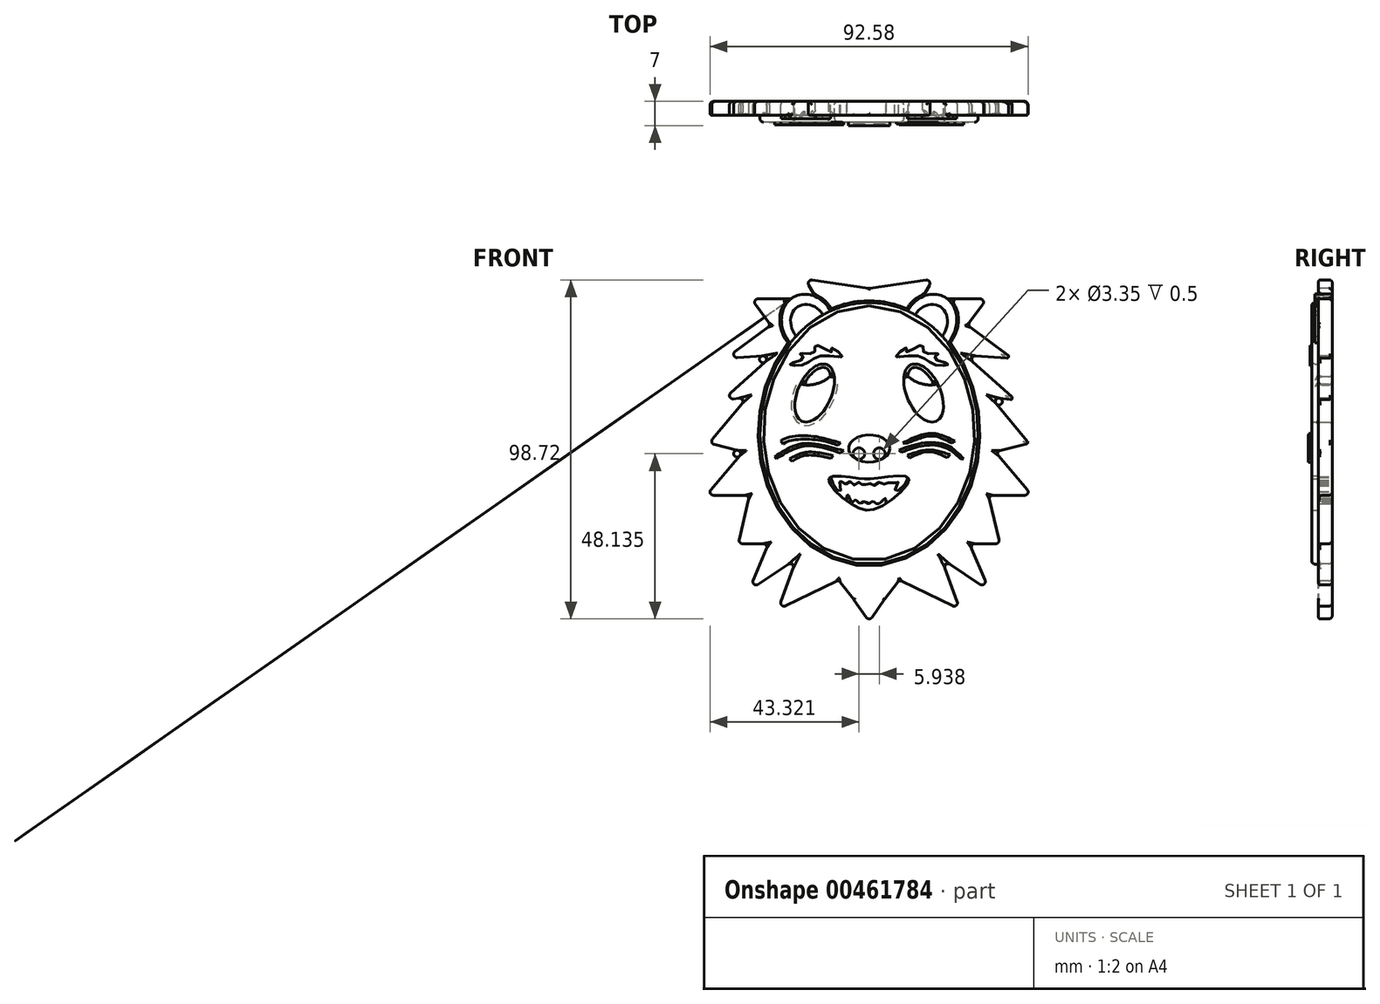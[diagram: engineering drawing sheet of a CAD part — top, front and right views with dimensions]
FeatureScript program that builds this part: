
annotation { "Feature Type Name" : "Feature", "Feature Type Description" : "" }
export const myFeature = defineFeature(function(context is Context, id is Id, definition is map)
    precondition{}
    {
        {
            var Q0;
            Q0=qCreatedBy(makeId("Front.planeOp"),FACE);
            var sketch = newSketch(context, id + "F0", { "sketchPlane" : qUnion([Q0])});
            skEllipse(sketch, "E0", {"center": v(0, 0) * mm, "majorRadius": 38.1 * mm, "minorRadius": 31.75 * mm, "majorAxis": v(0, 1)});
            skSolve(sketch);
        }
        {
            var Q0;
            Q0 = qSketchRegion(id + "F0", true);
            extrude(context, id + "F1", {"entities" : qUnion([Q0]), "depth" : 6 * mm});
        }
        {
            var Q0;
            Q0=makeQuery(id+"F1.opExtrude","CAP_FACE",FACE,{"disambiguationData":[OSD([sQuery(id+"F0.wireOp",EDGE,"E0")])],"isStart":false});
            var sketch = newSketch(context, id + "F2", { "sketchPlane" : qUnion([Q0])});
            skEllipse(sketch, "E1", {"center": v(-15.85, 11.73) * mm, "majorRadius": 9 * mm, "minorRadius": 4.9 * mm, "majorAxis": v(0.4, 0.91)});
            skEllipse(sketch, "E2.MirrorC", {"center": v(15.85, 11.73) * mm, "majorRadius": 9 * mm, "minorRadius": 4.9 * mm, "majorAxis": v(-0.4, 0.91)});
            skSolve(sketch);
        }
        {
            var Q0;
            Q0 = qSketchRegion(id + "F2", true);
            extrude(context, id + "F3", {"entities" : qUnion([Q0]), "operationType" : NewBodyOperationType.REMOVE, "oppositeDirection" : true, "depth" : 6 * mm});
        }
        {
            var Q0;
            Q0=qCreatedBy(makeId("Front.planeOp"),FACE);
            var sketch = newSketch(context, id + "F4", { "sketchPlane" : qUnion([Q0])});
            skEllipse(sketch, "E3", {"center": v(0, -4.43) * mm, "majorRadius": 6 * mm, "minorRadius": 4 * mm, "majorAxis": v(1, 0)});
            skSolve(sketch);
        }
        {
            var Q0;
            Q0 = qSketchRegion(id + "F4", true);
            extrude(context, id + "F5", {"entities" : qUnion([Q0]), "operationType" : NewBodyOperationType.ADD, "depth" : 7 * mm});
        }
        {
            var Q0;
            Q0=qCreatedBy(makeId("Front.planeOp"),FACE);
            var sketch = newSketch(context, id + "F6", { "sketchPlane" : qUnion([Q0])});
            skLineSegment(sketch, "E4", {"start": v(-18.6, 44.96) * mm, "end": v(-15.24, 39.17) * mm});
            skLineSegment(sketch, "E5", {"start": v(-15.24, 39.17) * mm, "end": v(-34.29, 39.17) * mm});
            skLineSegment(sketch, "E6", {"start": v(-34.29, 39.17) * mm, "end": v(-28.63, 31.48) * mm});
            skLineSegment(sketch, "E7", {"start": v(-28.63, 31.48) * mm, "end": v(-41.79, 21.8) * mm});
            skLineSegment(sketch, "E8", {"start": v(-41.79, 21.8) * mm, "end": v(-28.04, 22.78) * mm});
            skLineSegment(sketch, "E9", {"start": v(-28.04, 22.78) * mm, "end": v(-42.7, 9.6) * mm});
            skLineSegment(sketch, "E10", {"start": v(-42.7, 9.6) * mm, "end": v(-35.36, 10.58) * mm});
            skLineSegment(sketch, "E11", {"start": v(-35.36, 10.58) * mm, "end": v(-46.61, -2.9) * mm});
            skLineSegment(sketch, "E12", {"start": v(-46.61, -2.9) * mm, "end": v(-36.6, -5.33) * mm});
            skLineSegment(sketch, "E13", {"start": v(-36.6, -5.33) * mm, "end": v(-47.45, -18.05) * mm});
            skLineSegment(sketch, "E14", {"start": v(-38.1, -32.16) * mm, "end": v(-29.26, -32.16) * mm});
            skLineSegment(sketch, "E15", {"start": v(-29.26, -32.16) * mm, "end": v(-35.05, -45.87) * mm});
            skLineSegment(sketch, "E16", {"start": v(-35.05, -45.87) * mm, "end": v(-21.03, -36.42) * mm});
            skLineSegment(sketch, "E17", {"start": v(-21.03, -36.42) * mm, "end": v(-26.52, -51.36) * mm});
            skLineSegment(sketch, "E18", {"start": v(-26.52, -51.36) * mm, "end": v(-8.87, -42.69) * mm});
            skLineSegment(sketch, "E19", {"start": v(-8.87, -42.69) * mm, "end": v(-4.45, -48.4) * mm});
            skLineSegment(sketch, "E20", {"start": v(-4.45, -48.4) * mm, "end": v(0, -54.8) * mm});
            skLineSegment(sketch, "E21", {"start": v(0, -38.1) * mm, "end": v(-21.95, -23.62) * mm});
            skLineSegment(sketch, "E22", {"start": v(-21.95, -23.62) * mm, "end": v(-29.26, 0) * mm});
            skPoint(sketch, "E22.endSnap0", {"position": v(-31.75, 0) * mm});
            skLineSegment(sketch, "E23", {"start": v(-29.26, 0) * mm, "end": v(-24.03, 24.9) * mm});
            skLineSegment(sketch, "E24", {"start": v(-24.03, 24.9) * mm, "end": v(-8.87, 36.06) * mm});
            skLineSegment(sketch, "E25", {"start": v(-8.87, 36.06) * mm, "end": v(0, 38.1) * mm});
            skLineSegment(sketch, "E26", {"start": v(-47.45, -18.05) * mm, "end": v(-34.77, -18.05) * mm});
            skLineSegment(sketch, "E27", {"start": v(-34.77, -18.05) * mm, "end": v(-38.1, -32.16) * mm});
            skLineSegment(sketch, "E28.MirrorCS", {"start": v(18.6, 44.96) * mm, "end": v(15.24, 39.17) * mm});
            skLineSegment(sketch, "E29.MirrorCS", {"start": v(15.24, 39.17) * mm, "end": v(34.29, 39.17) * mm});
            skLineSegment(sketch, "E30.MirrorCS", {"start": v(34.29, 39.17) * mm, "end": v(28.63, 31.48) * mm});
            skLineSegment(sketch, "E31.MirrorCS", {"start": v(28.63, 31.48) * mm, "end": v(41.79, 21.8) * mm});
            skLineSegment(sketch, "E32.MirrorCS", {"start": v(41.79, 21.8) * mm, "end": v(28.04, 22.78) * mm});
            skLineSegment(sketch, "E33.MirrorCS", {"start": v(28.04, 22.78) * mm, "end": v(42.7, 9.6) * mm});
            skLineSegment(sketch, "E34.MirrorCS", {"start": v(42.7, 9.6) * mm, "end": v(35.36, 10.58) * mm});
            skLineSegment(sketch, "E35.MirrorCS", {"start": v(35.36, 10.58) * mm, "end": v(46.61, -2.9) * mm});
            skLineSegment(sketch, "E36.MirrorCS", {"start": v(36.6, -5.33) * mm, "end": v(47.45, -18.05) * mm});
            skLineSegment(sketch, "E37.MirrorCS", {"start": v(47.45, -18.05) * mm, "end": v(34.77, -18.05) * mm});
            skLineSegment(sketch, "E38.MirrorCS", {"start": v(38.1, -32.16) * mm, "end": v(29.26, -32.16) * mm});
            skLineSegment(sketch, "E39.MirrorCS", {"start": v(29.26, -32.16) * mm, "end": v(35.05, -45.87) * mm});
            skLineSegment(sketch, "E40.MirrorCS", {"start": v(35.05, -45.87) * mm, "end": v(21.03, -36.42) * mm});
            skLineSegment(sketch, "E41.MirrorCS", {"start": v(21.03, -36.42) * mm, "end": v(26.52, -51.36) * mm});
            skLineSegment(sketch, "E42.MirrorCS", {"start": v(26.52, -51.36) * mm, "end": v(8.87, -42.69) * mm});
            skLineSegment(sketch, "E43.MirrorCS", {"start": v(4.45, -48.4) * mm, "end": v(0, -54.8) * mm});
            skLineSegment(sketch, "E44.MirrorCS", {"start": v(8.87, -42.69) * mm, "end": v(4.45, -48.4) * mm});
            skLineSegment(sketch, "E45", {"start": v(34.77, -18.05) * mm, "end": v(38.1, -32.16) * mm});
            skLineSegment(sketch, "E46", {"start": v(0, -38.1) * mm, "end": v(22.36, -27.05) * mm});
            skLineSegment(sketch, "E47", {"start": v(46.61, -2.9) * mm, "end": v(36.6, -5.33) * mm});
            skLineSegment(sketch, "E48", {"start": v(29.66, 13.59) * mm, "end": v(22.36, -27.05) * mm});
            skLineSegment(sketch, "E49", {"start": v(-18.6, 44.96) * mm, "end": v(0, 42.21) * mm});
            skLineSegment(sketch, "E50", {"start": v(0, 42.21) * mm, "end": v(18.6, 44.96) * mm});
            skLineSegment(sketch, "E51", {"start": v(0, 38.1) * mm, "end": v(16.15, 31) * mm});
            skLineSegment(sketch, "E52", {"start": v(16.15, 31) * mm, "end": v(21.95, 22.78) * mm});
            skLineSegment(sketch, "E53", {"start": v(21.95, 22.78) * mm, "end": v(29.66, 13.59) * mm});
            skSolve(sketch);
        }
        {
            var Q0;
            Q0 = qSketchRegion(id + "F6", true);
            extrude(context, id + "F7", {"entities" : qUnion([Q0]), "operationType" : NewBodyOperationType.ADD, "depth" : 4 * mm});
        }
        {
            var Q0;
            Q0=qCreatedBy(makeId("Front.planeOp"),FACE);
            var sketch = newSketch(context, id + "F8", { "sketchPlane" : qUnion([Q0])});
            skEllipse(sketch, "E54", {"center": v(-15.73, 17.4) * mm, "majorRadius": 5.64 * mm, "minorRadius": 2.95 * mm, "majorAxis": v(0.95, 0.32)});
            skEllipse(sketch, "E55.MirrorC", {"center": v(15.73, 17.4) * mm, "majorRadius": 5.64 * mm, "minorRadius": 2.95 * mm, "majorAxis": v(-0.95, 0.32)});
            skSolve(sketch);
        }
        {
            var Q0;
            Q0 = qSketchRegion(id + "F8", true);
            extrude(context, id + "F9", {"entities" : qUnion([Q0]), "operationType" : NewBodyOperationType.ADD, "depth" : 4 * mm});
        }
        {
            var Q0;
            Q0=qCreatedBy(makeId("Front.planeOp"),FACE);
            var sketch = newSketch(context, id + "F10", { "sketchPlane" : qUnion([Q0])});
            skEllipse(sketch, "E56", {"center": v(-17.69, 31.9) * mm, "majorRadius": 8.9 * mm, "minorRadius": 7.53 * mm, "majorAxis": v(-0.45, 0.9)});
            skEllipse(sketch, "E57", {"center": v(-17.69, 31.9) * mm, "majorRadius": 5.85 * mm, "minorRadius": 4.97 * mm, "majorAxis": v(-0.46, 0.89)});
            skEllipse(sketch, "E58.MirrorC", {"center": v(17.69, 31.9) * mm, "majorRadius": 5.85 * mm, "minorRadius": 4.97 * mm, "majorAxis": v(0.46, 0.89)});
            skEllipse(sketch, "E59.MirrorC", {"center": v(17.69, 31.9) * mm, "majorRadius": 8.9 * mm, "minorRadius": 7.53 * mm, "majorAxis": v(0.45, 0.9)});
            skSolve(sketch);
        }
        {
            var Q0;
            Q0 = qSketchRegion(id + "F10", true);
            extrude(context, id + "F11", {"entities" : qUnion([Q0]), "operationType" : NewBodyOperationType.ADD, "depth" : 5 * mm});
        }
        {
            var Q0;
            Q0=qCreatedBy(makeId("Front.planeOp"),FACE);
            var sketch = newSketch(context, id + "F12", { "sketchPlane" : qUnion([Q0])});
            skFitSpline(sketch, "E60", {"points": [v(-11.75, -13.08) * mm, v(-4.98, -20.75) * mm, v(3.6, -21.2) * mm, v(11.55, -13.08) * mm, v(1.98, -13.08) * mm, v(-3.98, -12.99) * mm, v(-11.75, -13.08) * mm]});
            skSolve(sketch);
        }
        {
            var Q0;
            Q0 = qSketchRegion(id + "F12", true);
            extrude(context, id + "F13", {"entities" : qUnion([Q0]), "operationType" : NewBodyOperationType.REMOVE, "depth" : 6 * mm});
        }
        {
            var Q0;
            Q0=qCreatedBy(makeId("Front.planeOp"),FACE);
            var sketch = newSketch(context, id + "F14", { "sketchPlane" : qUnion([Q0])});
            skFitSpline(sketch, "E61", {"points": [v(-11.45, -12.13) * mm, v(-9.72, -16.03) * mm, v(-8.33, -16.93) * mm, v(-8.55, -13.58) * mm, v(-7.21, -14.86) * mm, v(-5.6, -14.03) * mm, v(-4.32, -15.09) * mm, v(-2.53, -14.14) * mm, v(-1.86, -15.25) * mm, v(0, -14.42) * mm, v(1.2, -15.25) * mm, v(3.04, -14.2) * mm, v(4.77, -14.92) * mm, v(6.1, -14.08) * mm, v(7.6, -14.7) * mm, v(8.61, -13.86) * mm, v(7.5, -16.76) * mm, v(9.95, -15.48) * mm, v(11.68, -11.35) * mm], "startDerivative": vector(17.07, -53.25) * mm, "endDerivative": vector(11.1, 53.91) * mm});
            skLineSegment(sketch, "E62", {"start": v(-11.45, -12.13) * mm, "end": v(11.68, -11.35) * mm});
            skFitSpline(sketch, "E63", {"points": [v(-5.88, -21.22) * mm, v(-6.54, -19.15) * mm, v(-6.2, -17.88) * mm, v(-4.98, -20.05) * mm, v(-3.98, -19.38) * mm, v(-2.64, -20.44) * mm, v(-1.36, -19.88) * mm, v(0, -20.5) * mm, v(0.92, -19.82) * mm, v(2.26, -20.55) * mm, v(3.7, -19.82) * mm, v(4.82, -18.99) * mm, v(4.32, -22.05) * mm, v(2.2, -23.61) * mm], "startDerivative": vector(-11.27, 24.17) * mm, "endDerivative": vector(-26.47, -9.23) * mm});
            skLineSegment(sketch, "E64", {"start": v(-5.88, -21.22) * mm, "end": v(2.2, -23.61) * mm});
            skSolve(sketch);
        }
        {
            var Q0;
            Q0 = qSketchRegion(id + "F14", true);
            extrude(context, id + "F15", {"entities" : qUnion([Q0]), "operationType" : NewBodyOperationType.ADD, "depth" : 4 * mm});
        }
        {
            var Q0;
            Q0=makeQuery(id+"F5.opExtrude","CAP_FACE",FACE,{"disambiguationData":[OSD([sQuery(id+"F4.wireOp",EDGE,"E3")])],"isStart":false});
            var sketch = newSketch(context, id + "F16", { "sketchPlane" : qUnion([Q0])});
            skCircle(sketch, "E65", {"center": v(-2.97, -5.91) * mm, "radius": 1.68 * mm});
            skCircle(sketch, "E66.MirrorC", {"center": v(2.97, -5.91) * mm, "radius": 1.68 * mm});
            skSolve(sketch);
        }
        {
            var Q0;
            Q0 = qSketchRegion(id + "F16", true);
            extrude(context, id + "F17", {"entities" : qUnion([Q0]), "operationType" : NewBodyOperationType.REMOVE, "oppositeDirection" : true, "depth" : .5 * mm});
        }
        {
            var Q0;
            Q0=makeQuery(id+"F2.imprint","IMPRINT",FACE,{"disambiguationData":[TD([[makeQuery(id+"F2.imprint","IMPRINT",EDGE,{"derivedFrom":sQuery(id+"F2.wireOp",EDGE,"E1")}),-1.0]])]});
            var sketch = newSketch(context, id + "F18", { "sketchPlane" : qUnion([Q0])});
            skFitSpline(sketch, "E67", {"points": [v(9.8, -2.85) * mm, v(17.8, 0) * mm, v(24.95, -2.25) * mm], "startDerivative": vector(15.7, 8.16) * mm, "endDerivative": vector(14.59, -7.12) * mm});
            skFitSpline(sketch, "E68", {"points": [v(-8.32, -2.73) * mm, v(-16.1, -0.89) * mm, v(-25.65, -2.24) * mm], "startDerivative": vector(-15.98, 3.58) * mm, "endDerivative": vector(-10.43, -9.33) * mm});
            skFitSpline(sketch, "E69", {"points": [v(-7.42, -5.03) * mm, v(-12.63, -3.68) * mm, v(-18.51, -2.91) * mm, v(-23.43, -4.36) * mm, v(-27.48, -6.77) * mm], "startDerivative": vector(-20.11, 5.43) * mm, "endDerivative": vector(-16.58, -10.79) * mm});
            skFitSpline(sketch, "E70", {"points": [v(8.77, -4.84) * mm, v(14.75, -3) * mm, v(20.92, -2.91) * mm, v(24.59, -4.65) * mm, v(27.58, -7.44) * mm], "startDerivative": vector(20.93, 7.75) * mm, "endDerivative": vector(12.9, -13.3) * mm});
            skFitSpline(sketch, "E71", {"points": [v(-10.5, -6.48) * mm, v(-18.32, -5.52) * mm, v(-23.14, -7.44) * mm], "startDerivative": vector(-15.1, 3.42) * mm, "endDerivative": vector(-10, -5.66) * mm});
            skFitSpline(sketch, "E72", {"points": [v(11.09, -6.38) * mm, v(17.55, -4.84) * mm, v(23.53, -6.2) * mm], "startDerivative": vector(12.78, 4.5) * mm, "endDerivative": vector(12.09, -4.17) * mm});
            skLineSegment(sketch, "E73", {"start": v(-25.65, -2.24) * mm, "end": v(-25.03, -3.06) * mm});
            skLineSegment(sketch, "E74", {"start": v(-8.32, -2.73) * mm, "end": v(-9.01, -3.54) * mm});
            skFitSpline(sketch, "E75", {"points": [v(-25.03, -3.06) * mm, v(-20.47, -1.77) * mm, v(-13.24, -2.24) * mm, v(-9.01, -3.54) * mm], "startDerivative": vector(13.32, 7.9) * mm, "endDerivative": vector(12.63, -4.67) * mm});
            skLineSegment(sketch, "E76", {"start": v(-27.48, -6.77) * mm, "end": v(-26.94, -7.38) * mm});
            skLineSegment(sketch, "E77", {"start": v(-7.42, -5.03) * mm, "end": v(-8.33, -5.81) * mm});
            skLineSegment(sketch, "E78", {"start": v(-10.5, -6.48) * mm, "end": v(-11.1, -7.31) * mm});
            skLineSegment(sketch, "E79", {"start": v(-23.14, -7.44) * mm, "end": v(-22.45, -8.17) * mm});
            skFitSpline(sketch, "E80", {"points": [v(-26.94, -7.38) * mm, v(-23.23, -5.17) * mm, v(-18.8, -3.74) * mm, v(-13.75, -4.1) * mm, v(-8.33, -5.81) * mm], "startDerivative": vector(15.33, 9.96) * mm, "endDerivative": vector(20.15, -7.26) * mm});
            skFitSpline(sketch, "E81", {"points": [v(-22.45, -8.17) * mm, v(-19.45, -6.67) * mm, v(-15.96, -6.38) * mm, v(-11.1, -7.31) * mm], "startDerivative": vector(9.45, 5.68) * mm, "endDerivative": vector(13.37, -3.16) * mm});
            skLineSegment(sketch, "E82", {"start": v(24.95, -2.25) * mm, "end": v(24.27, -2.85) * mm});
            skLineSegment(sketch, "E83", {"start": v(27.58, -7.44) * mm, "end": v(26.62, -7.44) * mm});
            skLineSegment(sketch, "E84", {"start": v(23.53, -6.2) * mm, "end": v(22.84, -7.1) * mm});
            skLineSegment(sketch, "E85", {"start": v(11.09, -6.38) * mm, "end": v(11.79, -7.17) * mm});
            skLineSegment(sketch, "E86", {"start": v(8.77, -4.84) * mm, "end": v(9.36, -5.53) * mm});
            skLineSegment(sketch, "E87", {"start": v(9.8, -2.85) * mm, "end": v(11.07, -2.85) * mm});
            skFitSpline(sketch, "E88", {"points": [v(11.07, -2.85) * mm, v(15.14, -1.32) * mm, v(19, -0.82) * mm, v(24.27, -2.85) * mm], "startDerivative": vector(12.65, 5.13) * mm, "endDerivative": vector(14.77, -7.34) * mm});
            skFitSpline(sketch, "E89", {"points": [v(9.36, -5.53) * mm, v(14.5, -3.89) * mm, v(19.28, -3.46) * mm, v(23.41, -4.74) * mm, v(26.62, -7.44) * mm], "startDerivative": vector(19.13, 6.9) * mm, "endDerivative": vector(12.69, -12.6) * mm});
            skFitSpline(sketch, "E90", {"points": [v(22.84, -7.1) * mm, v(18.78, -5.53) * mm, v(15.78, -5.53) * mm, v(11.79, -7.17) * mm], "startDerivative": vector(-11.93, 5.4) * mm, "endDerivative": vector(-11.74, -5.7) * mm});
            skSolve(sketch);
        }
        {
            var Q0;
            Q0 = qSketchRegion(id + "F18", true);
            extrude(context, id + "F19", {"entities" : qUnion([Q0]), "operationType" : NewBodyOperationType.ADD, "depth" : .8 * mm});
        }
        {
            var Q0;
            Q0=makeQuery(id+"F2.imprint","IMPRINT",FACE,{"disambiguationData":[TD([[makeQuery(id+"F2.imprint","IMPRINT",EDGE,{"derivedFrom":sQuery(id+"F2.wireOp",EDGE,"E1")}),-1.0]])]});
            var sketch = newSketch(context, id + "F20", { "sketchPlane" : qUnion([Q0])});
            skFitSpline(sketch, "E91", {"points": [v(-7.9, 22.54) * mm, v(-11.11, 24.93) * mm, v(-10.76, 23.74) * mm, v(-15.52, 25.64) * mm, v(-16, 23.5) * mm, v(-20.16, 23.26) * mm, v(-19.1, 21.95) * mm, v(-22.9, 20.16) * mm, v(-19.21, 19.92) * mm, v(-14.2, 22.54) * mm, v(-7.9, 22.54) * mm]});
            skFitSpline(sketch, "E92.MirrorC", {"points": [v(7.9, 22.54) * mm, v(11.11, 24.93) * mm, v(10.76, 23.74) * mm, v(15.52, 25.64) * mm, v(16, 23.5) * mm, v(20.16, 23.26) * mm, v(19.1, 21.95) * mm, v(22.9, 20.16) * mm, v(19.21, 19.92) * mm, v(14.2, 22.54) * mm, v(7.9, 22.54) * mm]});
            skSolve(sketch);
        }
        {
            var Q0;
            Q0 = qSketchRegion(id + "F20", true);
            extrude(context, id + "F21", {"entities" : qUnion([Q0]), "operationType" : NewBodyOperationType.ADD, "depth" : .5 * mm});
        }
        {
            var Q0;
            Q0=makeQuery(id+"F1.opExtrude","CAP_EDGE",EDGE,{"disambiguationData":[OSD([sQuery(id+"F0.wireOp",EDGE,"E0")])],"isStart":false});
            fillet(context, id + "F22", {"entities" : qUnion([Q0]), "radius" : 1 * mm, "tangentPropagation" : true, "allowEdgeOverflow" : false});
        }
        {
            var Q0;
            Q0=makeQuery(id+"F3.boolean.opBoolean","COPY",FACE,{"derivedFrom":makeQuery(id+"F3.opExtrude","SWEPT_FACE",FACE,{"disambiguationData":[OSD([sQuery(id+"F2.wireOp",EDGE,"E1")])]})});
            var Q1;
            Q1=makeQuery(id+"F3.boolean.opBoolean","COPY",FACE,{"derivedFrom":makeQuery(id+"F3.opExtrude","SWEPT_FACE",FACE,{"disambiguationData":[OSD([sQuery(id+"F2.wireOp",EDGE,"E2.MirrorC")])]})});
            fillet(context, id + "F23", {"entities" : qUnion([Q0, Q1]), "radius" : 1 * mm, "tangentPropagation" : true, "allowEdgeOverflow" : false});
        }
        {
            var Q0;
            Q0=makeQuery(id+"F9.opExtrude","SWEPT_FACE",FACE,{"disambiguationData":[OSD([sQuery(id+"F8.wireOp",EDGE,"E54")])]});
            var Q1;
            Q1=makeQuery(id+"F9.opExtrude","SWEPT_FACE",FACE,{"disambiguationData":[OSD([sQuery(id+"F8.wireOp",EDGE,"E55.MirrorC")])]});
            fillet(context, id + "F24", {"entities" : qUnion([Q0, Q1]), "radius" : 1 * mm, "tangentPropagation" : true, "allowEdgeOverflow" : false});
        }
        {
            var Q0;
            {var subQ0=sQuery(id+"F6.wireOp",EDGE,"E49");var subQ1=sQuery(id+"F6.wireOp",EDGE,"E28.MirrorCS");var subQ2=sQuery(id+"F6.wireOp",EDGE,"E50");var subQ3=sQuery(id+"F6.wireOp",EDGE,"E4");Q0=makeQuery(id+"F11.boolean.opBoolean","SPLIT",FACE,{"disambiguationData":[TD([makeQuery(id+"F7.opExtrude","SWEPT_FACE",FACE,{"disambiguationData":[OSD([subQ3])]})])],"derivedFrom":makeQuery(id+"F7.opExtrude","CAP_FACE",FACE,{"disambiguationData":[OSD([subQ3,sQuery(id+"F6.wireOp",EDGE,"E5"),sQuery(id+"F6.wireOp",EDGE,"E6"),sQuery(id+"F6.wireOp",EDGE,"E7"),sQuery(id+"F6.wireOp",EDGE,"E8"),sQuery(id+"F6.wireOp",EDGE,"E9"),sQuery(id+"F6.wireOp",EDGE,"E10"),sQuery(id+"F6.wireOp",EDGE,"E11"),sQuery(id+"F6.wireOp",EDGE,"E12"),sQuery(id+"F6.wireOp",EDGE,"E13"),sQuery(id+"F6.wireOp",EDGE,"E14"),sQuery(id+"F6.wireOp",EDGE,"E15"),sQuery(id+"F6.wireOp",EDGE,"E16"),sQuery(id+"F6.wireOp",EDGE,"E17"),sQuery(id+"F6.wireOp",EDGE,"E18"),sQuery(id+"F6.wireOp",EDGE,"E19"),sQuery(id+"F6.wireOp",EDGE,"E20"),sQuery(id+"F6.wireOp",EDGE,"E21"),sQuery(id+"F6.wireOp",EDGE,"E22"),sQuery(id+"F6.wireOp",EDGE,"E23"),sQuery(id+"F6.wireOp",EDGE,"E24"),sQuery(id+"F6.wireOp",EDGE,"E26"),sQuery(id+"F6.wireOp",EDGE,"E27"),subQ1,sQuery(id+"F6.wireOp",EDGE,"E29.MirrorCS"),sQuery(id+"F6.wireOp",EDGE,"E30.MirrorCS"),sQuery(id+"F6.wireOp",EDGE,"E31.MirrorCS"),sQuery(id+"F6.wireOp",EDGE,"E32.MirrorCS"),sQuery(id+"F6.wireOp",EDGE,"E33.MirrorCS"),sQuery(id+"F6.wireOp",EDGE,"E34.MirrorCS"),sQuery(id+"F6.wireOp",EDGE,"E35.MirrorCS"),sQuery(id+"F6.wireOp",EDGE,"E36.MirrorCS"),sQuery(id+"F6.wireOp",EDGE,"E37.MirrorCS"),sQuery(id+"F6.wireOp",EDGE,"E38.MirrorCS"),sQuery(id+"F6.wireOp",EDGE,"E39.MirrorCS"),sQuery(id+"F6.wireOp",EDGE,"E40.MirrorCS"),sQuery(id+"F6.wireOp",EDGE,"E41.MirrorCS"),sQuery(id+"F6.wireOp",EDGE,"E42.MirrorCS"),sQuery(id+"F6.wireOp",EDGE,"E43.MirrorCS"),sQuery(id+"F6.wireOp",EDGE,"E44.MirrorCS"),sQuery(id+"F6.wireOp",EDGE,"E45"),sQuery(id+"F6.wireOp",EDGE,"E46"),sQuery(id+"F6.wireOp",EDGE,"E47"),sQuery(id+"F6.wireOp",EDGE,"E48"),subQ0,subQ2,sQuery(id+"F6.wireOp",EDGE,"E25"),sQuery(id+"F6.wireOp",EDGE,"E51"),sQuery(id+"F6.wireOp",EDGE,"E52"),sQuery(id+"F6.wireOp",EDGE,"E53")])],"isStart":false})});}
            var Q1;
            {var subQ0=sQuery(id+"F6.wireOp",EDGE,"E27");var subQ1=sQuery(id+"F6.wireOp",EDGE,"E26");var subQ2=sQuery(id+"F6.wireOp",EDGE,"E20");var subQ3=sQuery(id+"F6.wireOp",EDGE,"E19");var subQ4=sQuery(id+"F6.wireOp",EDGE,"E17");var subQ5=sQuery(id+"F6.wireOp",EDGE,"E16");var subQ6=sQuery(id+"F6.wireOp",EDGE,"E15");var subQ7=sQuery(id+"F6.wireOp",EDGE,"E14");var subQ8=sQuery(id+"F6.wireOp",EDGE,"E31.MirrorCS");var subQ9=sQuery(id+"F6.wireOp",EDGE,"E7");var subQ10=sQuery(id+"F6.wireOp",EDGE,"E29.MirrorCS");var subQ11=sQuery(id+"F6.wireOp",EDGE,"E5");var subQ12=sQuery(id+"F6.wireOp",EDGE,"E30.MirrorCS");var subQ13=sQuery(id+"F6.wireOp",EDGE,"E6");var subQ14=sQuery(id+"F6.wireOp",EDGE,"E18");var subQ15=sQuery(id+"F6.wireOp",EDGE,"E9");var subQ16=sQuery(id+"F6.wireOp",EDGE,"E13");var subQ17=sQuery(id+"F6.wireOp",EDGE,"E8");var subQ18=sQuery(id+"F6.wireOp",EDGE,"E10");var subQ19=sQuery(id+"F6.wireOp",EDGE,"E11");var subQ20=sQuery(id+"F6.wireOp",EDGE,"E12");var subQ21=sQuery(id+"F6.wireOp",EDGE,"E32.MirrorCS");var subQ22=sQuery(id+"F6.wireOp",EDGE,"E33.MirrorCS");var subQ23=sQuery(id+"F6.wireOp",EDGE,"E34.MirrorCS");var subQ24=sQuery(id+"F6.wireOp",EDGE,"E35.MirrorCS");var subQ25=sQuery(id+"F6.wireOp",EDGE,"E36.MirrorCS");var subQ26=sQuery(id+"F6.wireOp",EDGE,"E37.MirrorCS");var subQ27=sQuery(id+"F6.wireOp",EDGE,"E38.MirrorCS");var subQ28=sQuery(id+"F6.wireOp",EDGE,"E39.MirrorCS");var subQ29=sQuery(id+"F6.wireOp",EDGE,"E40.MirrorCS");var subQ30=sQuery(id+"F6.wireOp",EDGE,"E41.MirrorCS");var subQ31=sQuery(id+"F6.wireOp",EDGE,"E42.MirrorCS");var subQ32=sQuery(id+"F6.wireOp",EDGE,"E43.MirrorCS");var subQ33=sQuery(id+"F6.wireOp",EDGE,"E44.MirrorCS");var subQ34=sQuery(id+"F6.wireOp",EDGE,"E45");var subQ35=sQuery(id+"F6.wireOp",EDGE,"E47");Q1=makeQuery(id+"F11.boolean.opBoolean","SPLIT",FACE,{"disambiguationData":[TD([makeQuery(id+"F7.opExtrude","SWEPT_FACE",FACE,{"disambiguationData":[OSD([subQ11])]})])],"derivedFrom":makeQuery(id+"F7.opExtrude","CAP_FACE",FACE,{"disambiguationData":[OSD([sQuery(id+"F6.wireOp",EDGE,"E4"),subQ11,subQ13,subQ9,subQ17,subQ15,subQ18,subQ19,subQ20,subQ16,subQ7,subQ6,subQ5,subQ4,subQ14,subQ3,subQ2,sQuery(id+"F6.wireOp",EDGE,"E21"),sQuery(id+"F6.wireOp",EDGE,"E22"),sQuery(id+"F6.wireOp",EDGE,"E23"),sQuery(id+"F6.wireOp",EDGE,"E24"),subQ1,subQ0,sQuery(id+"F6.wireOp",EDGE,"E28.MirrorCS"),subQ10,subQ12,subQ8,subQ21,subQ22,subQ23,subQ24,subQ25,subQ26,subQ27,subQ28,subQ29,subQ30,subQ31,subQ32,subQ33,subQ34,sQuery(id+"F6.wireOp",EDGE,"E46"),subQ35,sQuery(id+"F6.wireOp",EDGE,"E48"),sQuery(id+"F6.wireOp",EDGE,"E49"),sQuery(id+"F6.wireOp",EDGE,"E50"),sQuery(id+"F6.wireOp",EDGE,"E25"),sQuery(id+"F6.wireOp",EDGE,"E51"),sQuery(id+"F6.wireOp",EDGE,"E52"),sQuery(id+"F6.wireOp",EDGE,"E53")])],"isStart":false})});}
            var Q2;
            Q2=makeQuery(id+"F7.opExtrude","SWEPT_EDGE",EDGE,{"disambiguationData":[OSD([sQuery(id+"F6.wireOp",EDGE,"E31.MirrorCS"),sQuery(id+"F6.wireOp",EDGE,"E32.MirrorCS")])]});
            var Q3;
            Q3=makeQuery(id+"F7.opExtrude","SWEPT_EDGE",EDGE,{"disambiguationData":[OSD([sQuery(id+"F6.wireOp",EDGE,"E33.MirrorCS"),sQuery(id+"F6.wireOp",EDGE,"E34.MirrorCS")])]});
            var Q4;
            Q4=makeQuery(id+"F7.opExtrude","SWEPT_EDGE",EDGE,{"disambiguationData":[OSD([sQuery(id+"F6.wireOp",EDGE,"E35.MirrorCS"),sQuery(id+"F6.wireOp",EDGE,"E47")])]});
            fillet(context, id + "F25", {"entities" : qUnion([Q0, Q1, Q2, Q3, Q4]), "radius" : .5 * mm, "tangentPropagation" : true, "allowEdgeOverflow" : false});
        }
        {
            var Q0;
            Q0=makeQuery(id+"F7.opExtrude","SWEPT_FACE",FACE,{"disambiguationData":[OSD([sQuery(id+"F6.wireOp",EDGE,"E5")])]});
            var Q1;
            Q1=makeQuery(id+"F7.opExtrude","SWEPT_FACE",FACE,{"disambiguationData":[OSD([sQuery(id+"F6.wireOp",EDGE,"E6")])]});
            var Q2;
            Q2=makeQuery(id+"F7.opExtrude","SWEPT_FACE",FACE,{"disambiguationData":[OSD([sQuery(id+"F6.wireOp",EDGE,"E7")])]});
            var Q3;
            Q3=makeQuery(id+"F7.opExtrude","SWEPT_FACE",FACE,{"disambiguationData":[OSD([sQuery(id+"F6.wireOp",EDGE,"E8")])]});
            var Q4;
            Q4=makeQuery(id+"F7.opExtrude","SWEPT_FACE",FACE,{"disambiguationData":[OSD([sQuery(id+"F6.wireOp",EDGE,"E9")])]});
            var Q5;
            Q5=makeQuery(id+"F7.opExtrude","SWEPT_FACE",FACE,{"disambiguationData":[OSD([sQuery(id+"F6.wireOp",EDGE,"E10")])]});
            var Q6;
            Q6=makeQuery(id+"F7.opExtrude","SWEPT_FACE",FACE,{"disambiguationData":[OSD([sQuery(id+"F6.wireOp",EDGE,"E11")])]});
            var Q7;
            Q7=makeQuery(id+"F7.opExtrude","SWEPT_FACE",FACE,{"disambiguationData":[OSD([sQuery(id+"F6.wireOp",EDGE,"E12")])]});
            var Q8;
            Q8=makeQuery(id+"F7.opExtrude","SWEPT_FACE",FACE,{"disambiguationData":[OSD([sQuery(id+"F6.wireOp",EDGE,"E13")])]});
            var Q9;
            Q9=makeQuery(id+"F7.opExtrude","SWEPT_FACE",FACE,{"disambiguationData":[OSD([sQuery(id+"F6.wireOp",EDGE,"E26")])]});
            var Q10;
            Q10=makeQuery(id+"F7.opExtrude","SWEPT_FACE",FACE,{"disambiguationData":[OSD([sQuery(id+"F6.wireOp",EDGE,"E27")])]});
            var Q11;
            Q11=makeQuery(id+"F7.opExtrude","SWEPT_FACE",FACE,{"disambiguationData":[OSD([sQuery(id+"F6.wireOp",EDGE,"E14")])]});
            var Q12;
            Q12=makeQuery(id+"F7.opExtrude","SWEPT_FACE",FACE,{"disambiguationData":[OSD([sQuery(id+"F6.wireOp",EDGE,"E15")])]});
            var Q13;
            Q13=makeQuery(id+"F7.opExtrude","SWEPT_FACE",FACE,{"disambiguationData":[OSD([sQuery(id+"F6.wireOp",EDGE,"E16")])]});
            var Q14;
            Q14=makeQuery(id+"F7.opExtrude","SWEPT_FACE",FACE,{"disambiguationData":[OSD([sQuery(id+"F6.wireOp",EDGE,"E18")])]});
            var Q15;
            Q15=makeQuery(id+"F7.opExtrude","SWEPT_FACE",FACE,{"disambiguationData":[OSD([sQuery(id+"F6.wireOp",EDGE,"E19")])]});
            var Q16;
            Q16=makeQuery(id+"F7.opExtrude","SWEPT_FACE",FACE,{"disambiguationData":[OSD([sQuery(id+"F6.wireOp",EDGE,"E20")])]});
            var Q17;
            Q17=makeQuery(id+"F7.opExtrude","SWEPT_FACE",FACE,{"disambiguationData":[OSD([sQuery(id+"F6.wireOp",EDGE,"E17")])]});
            var Q18;
            Q18=makeQuery(id+"F7.opExtrude","SWEPT_FACE",FACE,{"disambiguationData":[OSD([sQuery(id+"F6.wireOp",EDGE,"E43.MirrorCS")])]});
            var Q19;
            Q19=makeQuery(id+"F7.opExtrude","SWEPT_FACE",FACE,{"disambiguationData":[OSD([sQuery(id+"F6.wireOp",EDGE,"E44.MirrorCS")])]});
            var Q20;
            Q20=makeQuery(id+"F7.opExtrude","SWEPT_FACE",FACE,{"disambiguationData":[OSD([sQuery(id+"F6.wireOp",EDGE,"E42.MirrorCS")])]});
            var Q21;
            Q21=makeQuery(id+"F7.opExtrude","SWEPT_FACE",FACE,{"disambiguationData":[OSD([sQuery(id+"F6.wireOp",EDGE,"E41.MirrorCS")])]});
            var Q22;
            Q22=makeQuery(id+"F7.opExtrude","SWEPT_FACE",FACE,{"disambiguationData":[OSD([sQuery(id+"F6.wireOp",EDGE,"E40.MirrorCS")])]});
            var Q23;
            Q23=makeQuery(id+"F7.opExtrude","SWEPT_FACE",FACE,{"disambiguationData":[OSD([sQuery(id+"F6.wireOp",EDGE,"E39.MirrorCS")])]});
            var Q24;
            Q24=makeQuery(id+"F7.opExtrude","SWEPT_FACE",FACE,{"disambiguationData":[OSD([sQuery(id+"F6.wireOp",EDGE,"E38.MirrorCS")])]});
            var Q25;
            Q25=makeQuery(id+"F7.opExtrude","SWEPT_FACE",FACE,{"disambiguationData":[OSD([sQuery(id+"F6.wireOp",EDGE,"E45")])]});
            var Q26;
            Q26=makeQuery(id+"F7.opExtrude","SWEPT_FACE",FACE,{"disambiguationData":[OSD([sQuery(id+"F6.wireOp",EDGE,"E37.MirrorCS")])]});
            var Q27;
            Q27=makeQuery(id+"F7.opExtrude","SWEPT_FACE",FACE,{"disambiguationData":[OSD([sQuery(id+"F6.wireOp",EDGE,"E50")])]});
            var Q28;
            Q28=makeQuery(id+"F7.opExtrude","SWEPT_FACE",FACE,{"disambiguationData":[OSD([sQuery(id+"F6.wireOp",EDGE,"E49")])]});
            var Q29;
            Q29=makeQuery(id+"F7.opExtrude","SWEPT_FACE",FACE,{"disambiguationData":[OSD([sQuery(id+"F6.wireOp",EDGE,"E29.MirrorCS")])]});
            var Q30;
            Q30=makeQuery(id+"F7.opExtrude","SWEPT_FACE",FACE,{"disambiguationData":[OSD([sQuery(id+"F6.wireOp",EDGE,"E31.MirrorCS")])]});
            var Q31;
            Q31=makeQuery(id+"F7.opExtrude","SWEPT_FACE",FACE,{"disambiguationData":[OSD([sQuery(id+"F6.wireOp",EDGE,"E33.MirrorCS")])]});
            var Q32;
            Q32=makeQuery(id+"F7.opExtrude","SWEPT_FACE",FACE,{"disambiguationData":[OSD([sQuery(id+"F6.wireOp",EDGE,"E35.MirrorCS")])]});
            var Q33;
            Q33=makeQuery(id+"F7.opExtrude","SWEPT_FACE",FACE,{"disambiguationData":[OSD([sQuery(id+"F6.wireOp",EDGE,"E36.MirrorCS")])]});
            var Q34;
            Q34=makeQuery(id+"F7.opExtrude","SWEPT_FACE",FACE,{"disambiguationData":[OSD([sQuery(id+"F6.wireOp",EDGE,"E47")])]});
            var Q35;
            Q35=makeQuery(id+"F7.opExtrude","SWEPT_FACE",FACE,{"disambiguationData":[OSD([sQuery(id+"F6.wireOp",EDGE,"E34.MirrorCS")])]});
            var Q36;
            Q36=makeQuery(id+"F7.opExtrude","SWEPT_FACE",FACE,{"disambiguationData":[OSD([sQuery(id+"F6.wireOp",EDGE,"E32.MirrorCS")])]});
            var Q37;
            Q37=makeQuery(id+"F7.opExtrude","SWEPT_FACE",FACE,{"disambiguationData":[OSD([sQuery(id+"F6.wireOp",EDGE,"E30.MirrorCS")])]});
            fillet(context, id + "F26", {"entities" : qUnion([Q0, Q1, Q2, Q3, Q4, Q5, Q6, Q7, Q8, Q9, Q10, Q11, Q12, Q13, Q14, Q15, Q16, Q17, Q18, Q19, Q20, Q21, Q22, Q23, Q24, Q25, Q26, Q27, Q28, Q29, Q30, Q31, Q32, Q33, Q34, Q35, Q36, Q37]), "radius" : 1 * mm, "tangentPropagation" : true, "allowEdgeOverflow" : false});
        }
    });
